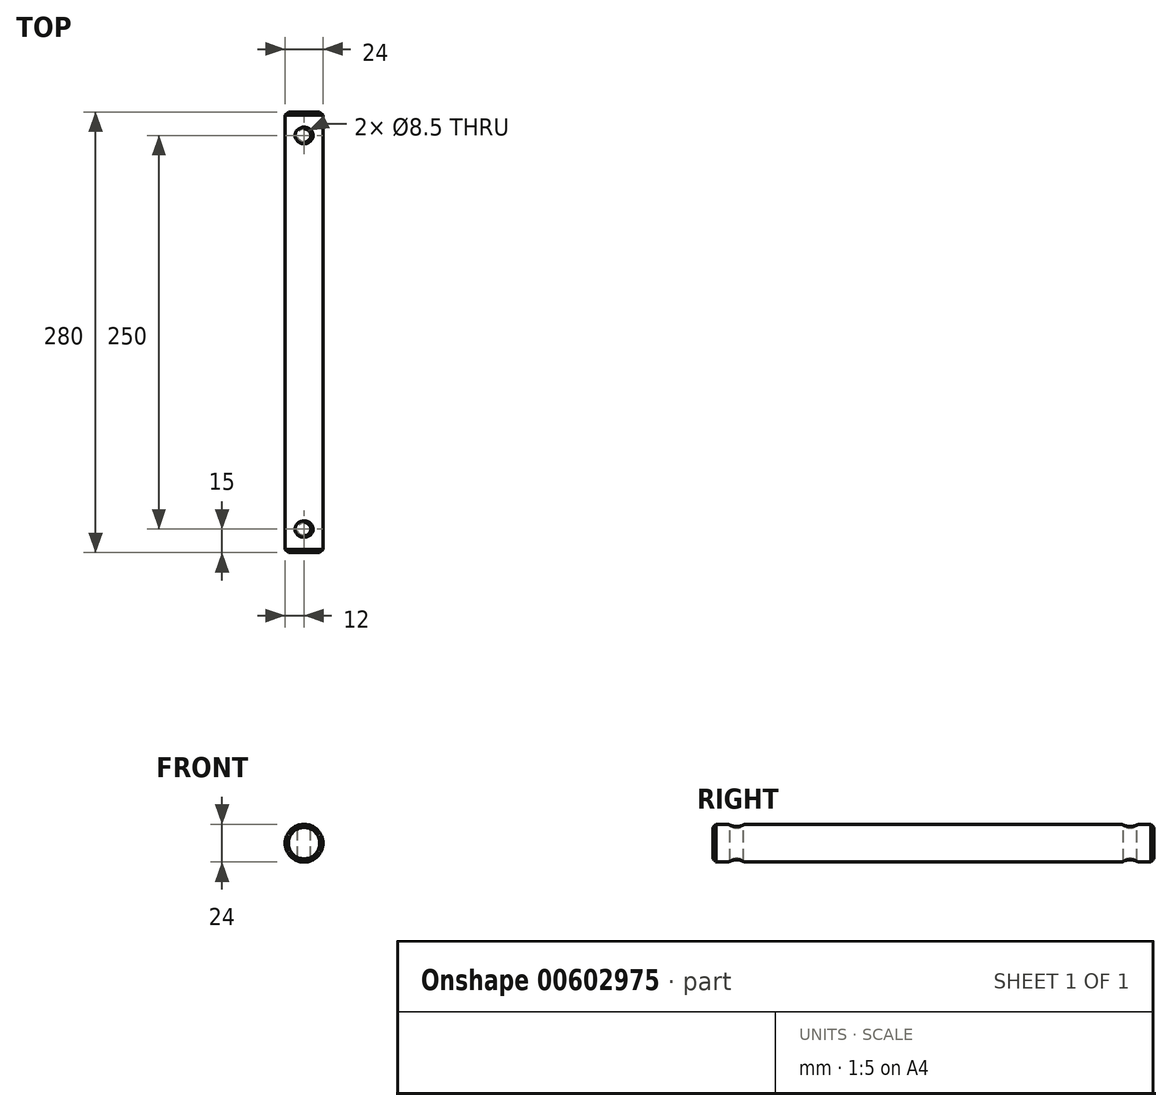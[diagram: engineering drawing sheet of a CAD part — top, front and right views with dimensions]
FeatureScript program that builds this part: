
annotation { "Feature Type Name" : "Feature", "Feature Type Description" : "" }
export const myFeature = defineFeature(function(context is Context, id is Id, definition is map)
    precondition{}
    {
        {
            var Q0;
            Q0=qCreatedBy(makeId("Front.planeOp"),FACE);
            var sketch = newSketch(context, id + "F0", { "sketchPlane" : qUnion([Q0])});
            skCircle(sketch, "E0", {"center": v(0, 0) * mm, "radius": 12 * mm});
            skSolve(sketch);
        }
        {
            var Q0;
            Q0=makeQuery(id+"F0.imprint","IMPRINT",FACE,{"disambiguationData":[TD([[makeQuery(id+"F0.imprint","IMPRINT",EDGE,{"derivedFrom":sQuery(id+"F0.wireOp",EDGE,"E0")}),1.0]])]});
            var Q1;
            Q1=sQuery(id+"F0.wireOp",EDGE,"E0");
            extrude(context, id + "F1", {"entities" : qUnion([Q0]), "surfaceEntities" : qUnion([Q1]), "endBound" : BoundingType.SYMMETRIC, "depth" : 280 * mm, "offsetDistance" : 25 * mm});
        }
        {
            var Q0;
            Q0=makeQuery(id+"F1.opExtrude","CAP_EDGE",EDGE,{"disambiguationData":[OSD([sQuery(id+"F0.wireOp",EDGE,"E0")])],"isStart":true});
            chamfer(context, id + "F2", {"entities" : qUnion([Q0]), "width" : 2 * mm, "tangentPropagation" : true});
        }
        {
            var Q0;
            Q0=makeQuery(id+"F1.opExtrude","CAP_EDGE",EDGE,{"disambiguationData":[OSD([sQuery(id+"F0.wireOp",EDGE,"E0")])],"isStart":false});
            chamfer(context, id + "F3", {"entities" : qUnion([Q0]), "width" : 2 * mm, "tangentPropagation" : true});
        }
        {
            var Q0;
            Q0=qCreatedBy(makeId("Top.planeOp"),FACE);
            var sketch = newSketch(context, id + "F4", { "sketchPlane" : qUnion([Q0])});
            skLineSegment(sketch, "E1", {"start": v(0, -93.47) * mm, "end": v(0, 94.1) * mm});
            skPoint(sketch, "E2", {"position": v(0, 125) * mm});
            skLineSegment(sketch, "E3", {"start": v(0, -136.9) * mm, "end": v(0, -41.43) * mm});
            skPoint(sketch, "E4", {"position": v(0, -125) * mm});
            skCircle(sketch, "E5", {"center": v(0, -125) * mm, "radius": 4.25 * mm});
            skCircle(sketch, "E6", {"center": v(0, 125) * mm, "radius": 4.25 * mm});
            skSolve(sketch);
        }
        {
            var Q0;
            Q0 = qSketchRegion(id + "F4", true);
            extrude(context, id + "F5", {"entities" : qUnion([Q0]), "operationType" : NewBodyOperationType.REMOVE, "endBound" : BoundingType.SYMMETRIC, "oppositeDirection" : true, "depth" : 24 * mm, "offsetDistance" : 25 * mm});
        }
        {
            var Q0;
            Q0=makeQuery(id+"F5.boolean.opBoolean","INTERSECT",EDGE,{"disambiguationData":[OD(1.0)],"derivedFrom":[makeQuery(id+"F1.opExtrude","SWEPT_FACE",FACE,{"disambiguationData":[OSD([sQuery(id+"F0.wireOp",EDGE,"E0")])]}),makeQuery(id+"F5.opExtrude","SWEPT_FACE",FACE,{"disambiguationData":[OSD([sQuery(id+"F4.wireOp",EDGE,"E5")])]})]});
            chamfer(context, id + "F6", {"entities" : qUnion([Q0]), "width" : 1 * mm, "tangentPropagation" : true});
        }
        {
            var Q0;
            Q0=makeQuery(id+"F5.boolean.opBoolean","INTERSECT",EDGE,{"disambiguationData":[OD(1.0)],"derivedFrom":[makeQuery(id+"F1.opExtrude","SWEPT_FACE",FACE,{"disambiguationData":[OSD([sQuery(id+"F0.wireOp",EDGE,"E0")])]}),makeQuery(id+"F5.opExtrude","SWEPT_FACE",FACE,{"disambiguationData":[OSD([sQuery(id+"F4.wireOp",EDGE,"E6")])]})]});
            chamfer(context, id + "F7", {"entities" : qUnion([Q0]), "width" : 1 * mm, "tangentPropagation" : true});
        }
        {
            var Q0;
            Q0=makeQuery(id+"F5.boolean.opBoolean","INTERSECT",EDGE,{"disambiguationData":[OD(0.0)],"derivedFrom":[makeQuery(id+"F1.opExtrude","SWEPT_FACE",FACE,{"disambiguationData":[OSD([sQuery(id+"F0.wireOp",EDGE,"E0")])]}),makeQuery(id+"F5.opExtrude","SWEPT_FACE",FACE,{"disambiguationData":[OSD([sQuery(id+"F4.wireOp",EDGE,"E6")])]})]});
            var Q1;
            Q1=makeQuery(id+"F5.boolean.opBoolean","INTERSECT",EDGE,{"disambiguationData":[OD(0.0)],"derivedFrom":[makeQuery(id+"F1.opExtrude","SWEPT_FACE",FACE,{"disambiguationData":[OSD([sQuery(id+"F0.wireOp",EDGE,"E0")])]}),makeQuery(id+"F5.opExtrude","SWEPT_FACE",FACE,{"disambiguationData":[OSD([sQuery(id+"F4.wireOp",EDGE,"E5")])]})]});
            chamfer(context, id + "F8", {"entities" : qUnion([Q0, Q1]), "width" : 1 * mm, "tangentPropagation" : true});
        }
    });
